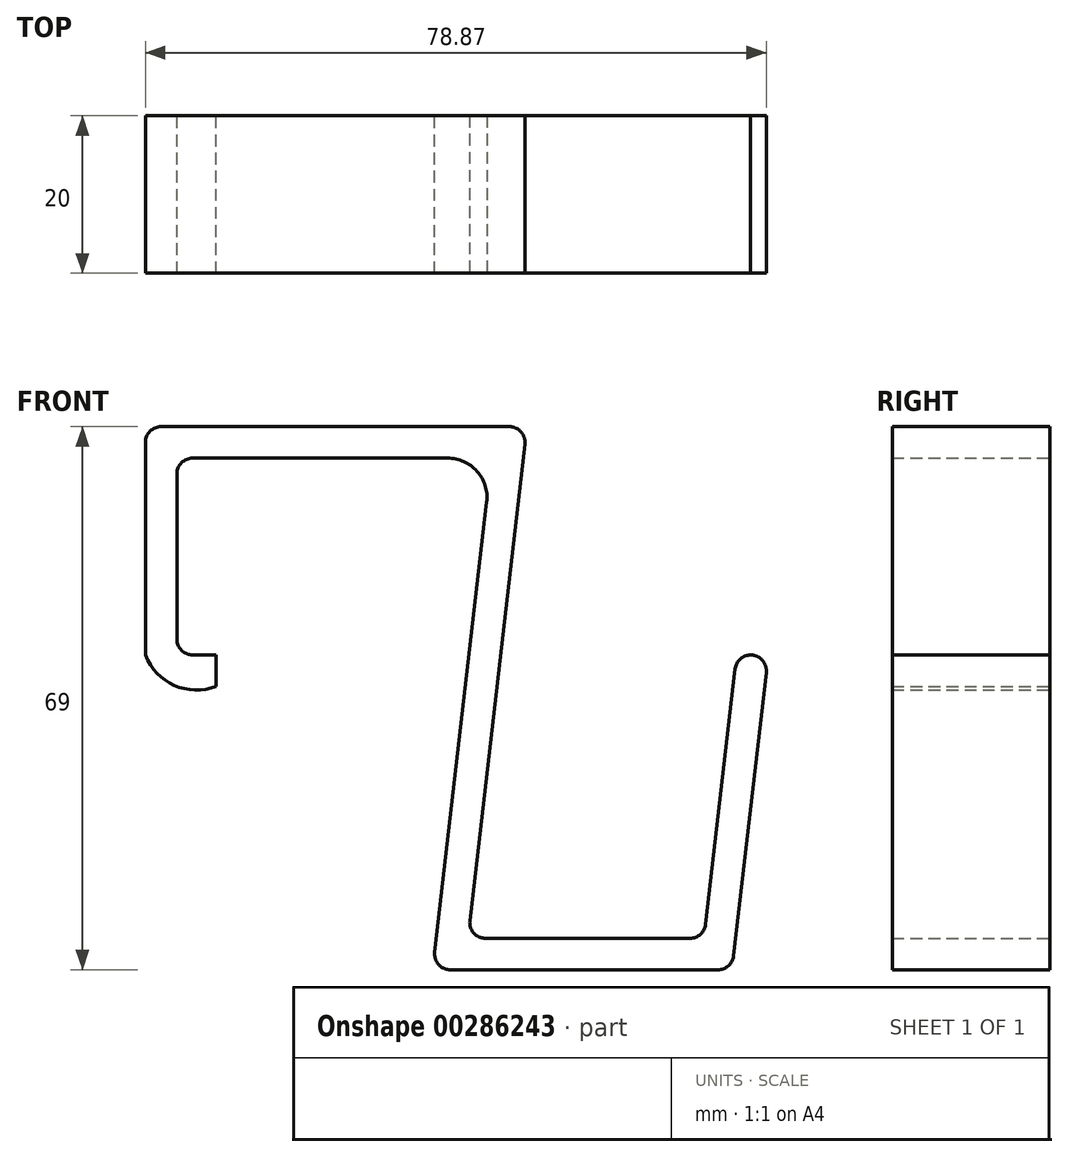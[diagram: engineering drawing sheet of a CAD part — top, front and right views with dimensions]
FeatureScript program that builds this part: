
annotation { "Feature Type Name" : "Feature", "Feature Type Description" : "" }
export const myFeature = defineFeature(function(context is Context, id is Id, definition is map)
    precondition{}
    {
        {
            var Q0;
            Q0=qCreatedBy(makeId("Front.planeOp"),FACE);
            var sketch = newSketch(context, id + "F0", { "sketchPlane" : qUnion([Q0])});
            skLineSegment(sketch, "E0", {"start": v(-24, 0) * mm, "end": v(-24, 29) * mm});
            skLineSegment(sketch, "E1", {"start": v(-24, 29) * mm, "end": v(24.46, 29) * mm});
            skLineSegment(sketch, "E2", {"start": v(24.46, 29) * mm, "end": v(16.96, -36) * mm});
            skLineSegment(sketch, "E3", {"start": v(16.96, -36) * mm, "end": v(46.96, -36) * mm});
            skLineSegment(sketch, "E4", {"start": v(46.96, -36) * mm, "end": v(51.11, 0) * mm});
            skLineSegment(sketch, "E5", {"start": v(51.11, 0) * mm, "end": v(55.11, 0) * mm});
            skLineSegment(sketch, "E6", {"start": v(55.11, 0) * mm, "end": v(50.5, -40) * mm});
            skLineSegment(sketch, "E7", {"start": v(50.5, -40) * mm, "end": v(12.5, -40) * mm});
            skLineSegment(sketch, "E8", {"start": v(12.5, -40) * mm, "end": v(20, 25) * mm});
            skLineSegment(sketch, "E9", {"start": v(20, 25) * mm, "end": v(-20, 25) * mm});
            skLineSegment(sketch, "E10", {"start": v(-20, 25) * mm, "end": v(-20, 0) * mm});
            skLineSegment(sketch, "E11", {"start": v(-20, 0) * mm, "end": v(-24, 0) * mm});
            skLineSegment(sketch, "E12", {"start": v(-15, -4) * mm, "end": v(-15, 0) * mm});
            skLineSegment(sketch, "E13", {"start": v(-15, 0) * mm, "end": v(-20, 0) * mm});
            skArc(sketch, "E14", {"start": v(-24, 0) * mm, "mid": v(-20.33, -3.86) * mm, "end": v(-15, -4) * mm});
            skSolve(sketch);
        }
        {
            var Q0;
            Q0=qSketchRegion(id+"F0",true);
            extrude(context, id + "F1", {"entities" : qUnion([Q0]), "depth" : 20 * mm});
        }
        {
            var Q0;
            Q0=makeQuery(id+"F1.opExtrude","SWEPT_EDGE",EDGE,{"disambiguationData":[OSD([sQuery(id+"F0.wireOp",EDGE,"E10"),sQuery(id+"F0.wireOp",EDGE,"E11"),sQuery(id+"F0.wireOp",EDGE,"E13")])]});
            var Q1;
            Q1=makeQuery(id+"F1.opExtrude","SWEPT_EDGE",EDGE,{"disambiguationData":[OSD([sQuery(id+"F0.wireOp",EDGE,"E9"),sQuery(id+"F0.wireOp",EDGE,"E10")])]});
            var Q2;
            Q2=makeQuery(id+"F1.opExtrude","SWEPT_EDGE",EDGE,{"disambiguationData":[OSD([sQuery(id+"F0.wireOp",EDGE,"E2"),sQuery(id+"F0.wireOp",EDGE,"E3")])]});
            var Q3;
            Q3=makeQuery(id+"F1.opExtrude","SWEPT_EDGE",EDGE,{"disambiguationData":[OSD([sQuery(id+"F0.wireOp",EDGE,"E3"),sQuery(id+"F0.wireOp",EDGE,"E4")])]});
            fillet(context, id + "F2", {"entities" : qUnion([Q0, Q1, Q2, Q3]), "radius" : 2 * mm, "tangentPropagation" : true, "allowEdgeOverflow" : false});
        }
        {
            var Q0;
            Q0=makeQuery(id+"F1.opExtrude","SWEPT_EDGE",EDGE,{"disambiguationData":[OSD([sQuery(id+"F0.wireOp",EDGE,"E0"),sQuery(id+"F0.wireOp",EDGE,"E1")])]});
            var Q1;
            Q1=makeQuery(id+"F1.opExtrude","SWEPT_EDGE",EDGE,{"disambiguationData":[OSD([sQuery(id+"F0.wireOp",EDGE,"E1"),sQuery(id+"F0.wireOp",EDGE,"E2")])]});
            var Q2;
            Q2=makeQuery(id+"F1.opExtrude","SWEPT_EDGE",EDGE,{"disambiguationData":[OSD([sQuery(id+"F0.wireOp",EDGE,"E7"),sQuery(id+"F0.wireOp",EDGE,"E8")])]});
            var Q3;
            Q3=makeQuery(id+"F1.opExtrude","SWEPT_EDGE",EDGE,{"disambiguationData":[OSD([sQuery(id+"F0.wireOp",EDGE,"E6"),sQuery(id+"F0.wireOp",EDGE,"E7")])]});
            var Q4;
            Q4=makeQuery(id+"F1.opExtrude","SWEPT_EDGE",EDGE,{"disambiguationData":[OSD([sQuery(id+"F0.wireOp",EDGE,"E4"),sQuery(id+"F0.wireOp",EDGE,"E5")])]});
            var Q5;
            Q5=makeQuery(id+"F1.opExtrude","SWEPT_EDGE",EDGE,{"disambiguationData":[OSD([sQuery(id+"F0.wireOp",EDGE,"E5"),sQuery(id+"F0.wireOp",EDGE,"E6")])]});
            fillet(context, id + "F3", {"entities" : qUnion([Q0, Q1, Q2, Q3, Q4, Q5]), "radius" : 2 * mm, "tangentPropagation" : true, "allowEdgeOverflow" : false});
        }
        {
            var Q0;
            Q0=makeQuery(id+"F1.opExtrude","SWEPT_EDGE",EDGE,{"disambiguationData":[OSD([sQuery(id+"F0.wireOp",EDGE,"E8"),sQuery(id+"F0.wireOp",EDGE,"E9")])]});
            fillet(context, id + "F4", {"entities" : qUnion([Q0]), "radius" : 5 * mm, "tangentPropagation" : true, "allowEdgeOverflow" : false});
        }
    });
